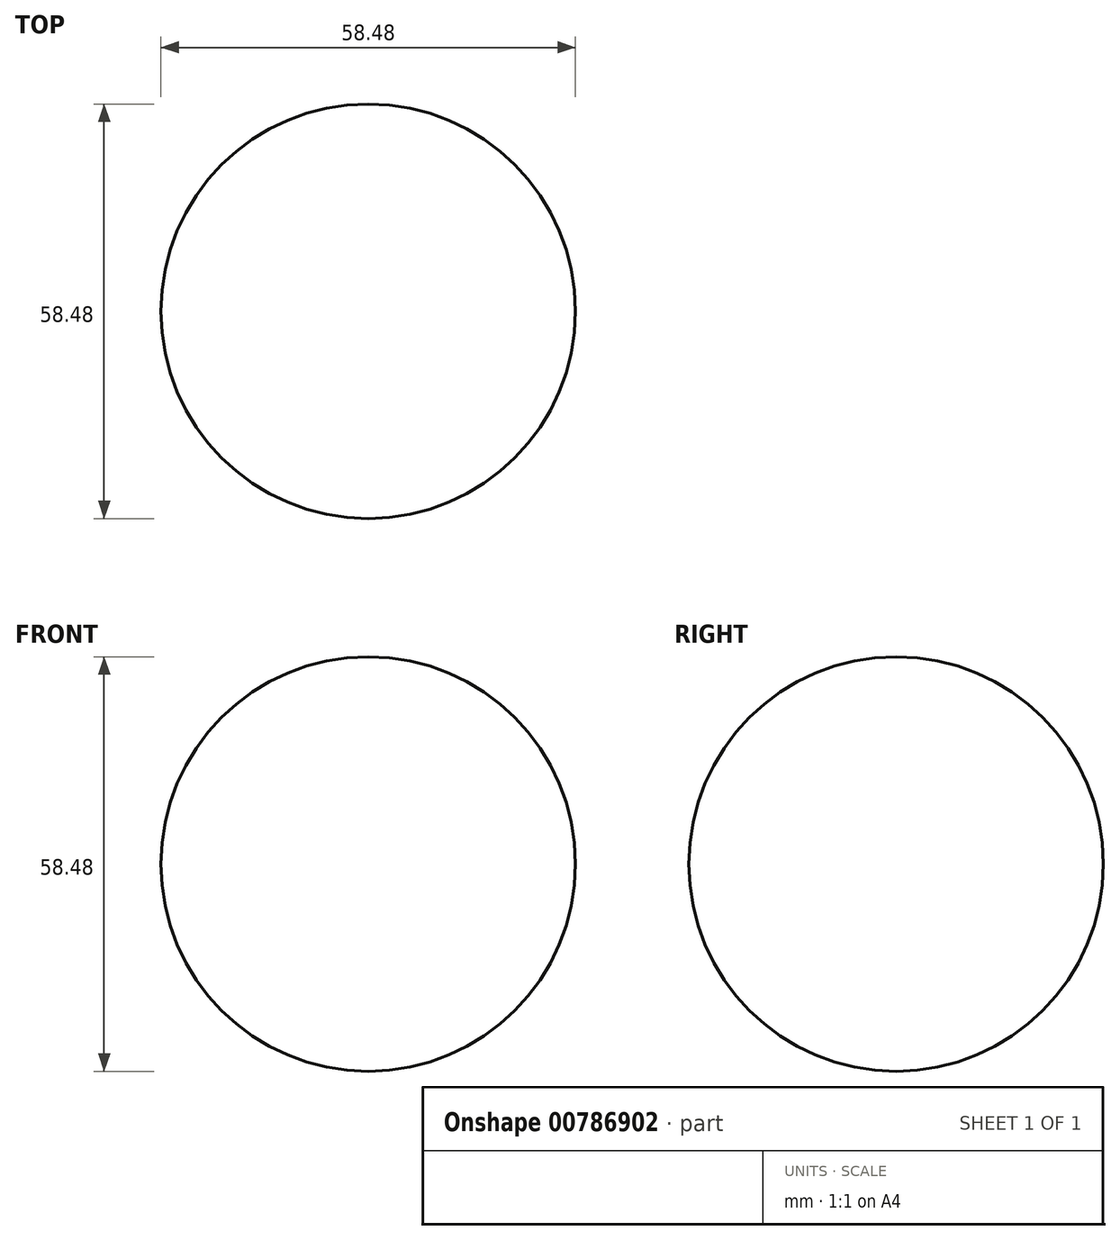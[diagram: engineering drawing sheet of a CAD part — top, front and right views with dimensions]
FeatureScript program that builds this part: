
annotation { "Feature Type Name" : "Feature", "Feature Type Description" : "" }
export const myFeature = defineFeature(function(context is Context, id is Id, definition is map)
    precondition{}
    {
        {
            var Q0;
            Q0=qCreatedBy(makeId("Front.planeOp"),FACE);
            var sketch = newSketch(context, id + "F0", { "sketchPlane" : qUnion([Q0])});
            skCircle(sketch, "E0", {"center": v(0, 0) * mm, "radius": 29.24 * mm});
            skLineSegment(sketch, "E1", {"start": v(0, 48.57) * mm, "end": v(0, -48.23) * mm});
            skSolve(sketch);
        }
        {
            var Q0;
            {var subQ0=sQuery(id+"F0.wireOp",EDGE,"E1");var subQ1=sQuery(id+"F0.wireOp",EDGE,"E0");var subQ2=makeQuery(id+"F0.imprint","INTERSECT",VERTEX,{"disambiguationData":[OD(0.0)],"derivedFrom":[subQ1,subQ0]});Q0=makeQuery(id+"F0.imprint","IMPRINT",FACE,{"disambiguationData":[TD([[makeQuery(id+"F0.imprint","IMPRINT",EDGE,{"disambiguationData":[TD([[subQ2,-1.0]])],"derivedFrom":subQ1}),1.0]])]});}
            var Q1;
            Q1=sQuery(id+"F0.wireOp",EDGE,"E1");
            revolve(context, id + "F1", {"surfaceOperationType" : NewSurfaceOperationType.NEW, "entities" : qUnion([Q0]), "axis" : qUnion([Q1]), "revolveType" : RevolveType.FULL});
        }
    });
